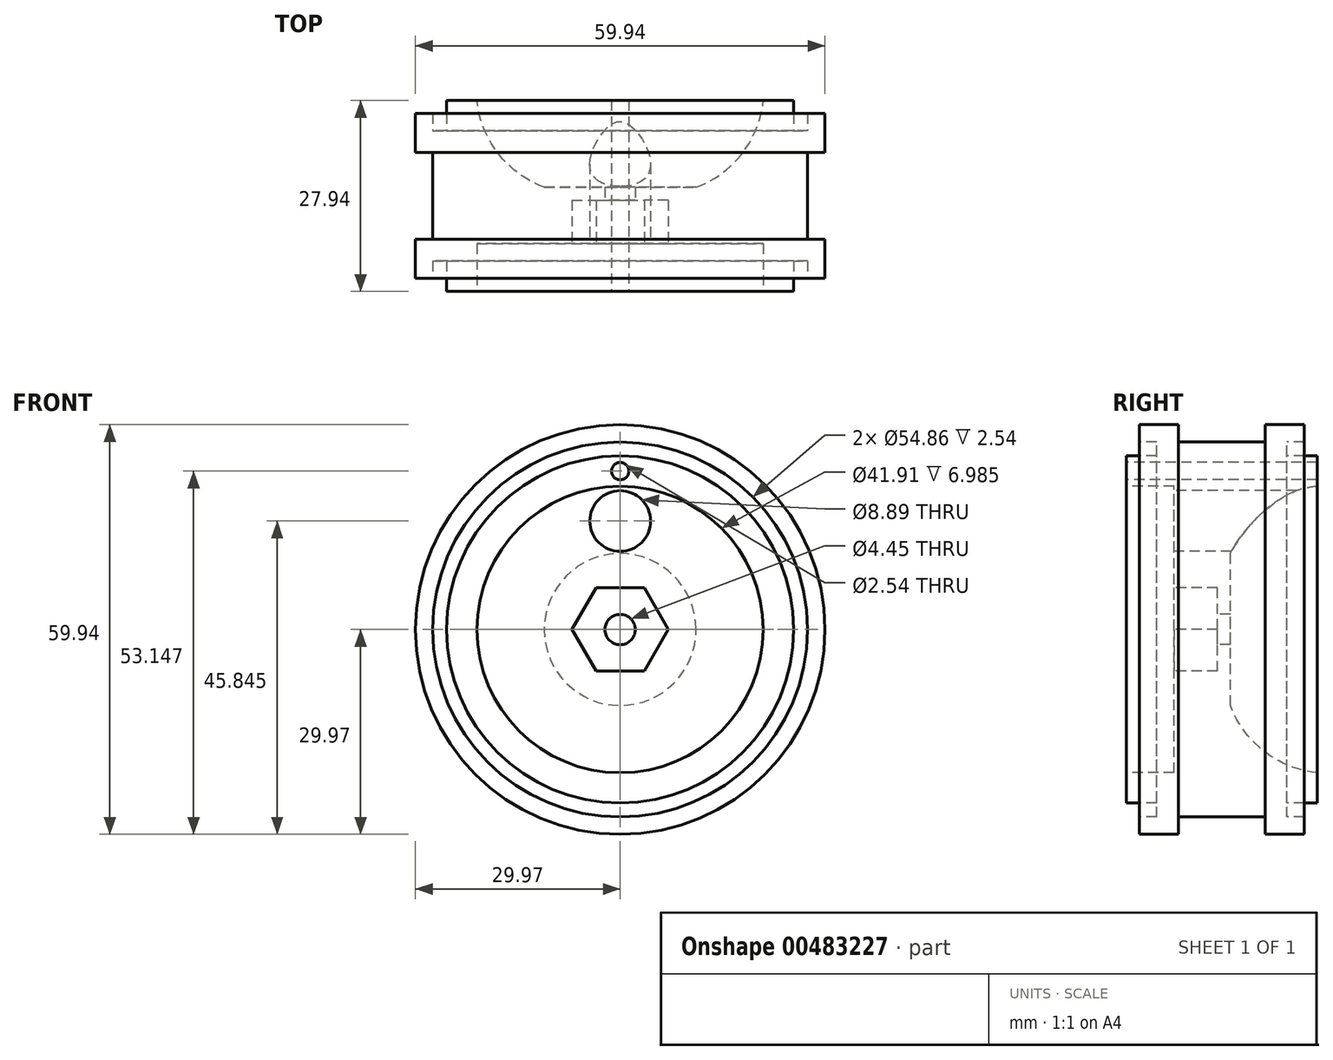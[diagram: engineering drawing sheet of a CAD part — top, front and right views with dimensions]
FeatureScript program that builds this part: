
annotation { "Feature Type Name" : "Feature", "Feature Type Description" : "" }
export const myFeature = defineFeature(function(context is Context, id is Id, definition is map)
    precondition{}
    {
        {
            var Q0;
            Q0=qCreatedBy(makeId("Front.planeOp"),FACE);
            var sketch = newSketch(context, id + "F0", { "sketchPlane" : qUnion([Q0])});
            skCircle(sketch, "E0", {"center": v(0, 0) * mm, "radius": 11.11 * mm});
            skSolve(sketch);
        }
        {
            var Q0;
            Q0=makeQuery(id+"F0.imprint","IMPRINT",FACE,{"disambiguationData":[TD([[makeQuery(id+"F0.imprint","IMPRINT",EDGE,{"derivedFrom":sQuery(id+"F0.wireOp",EDGE,"E0")}),1.0]])]});
            extrude(context, id + "F1", {"entities" : qUnion([Q0]), "depth" : 8.25 * mm});
        }
        {
            var Q0;
            Q0=qCreatedBy(makeId("Right.planeOp"),FACE);
            var sketch = newSketch(context, id + "F2", { "sketchPlane" : qUnion([Q0])});
            skLineSegment(sketch, "E1", {"start": v(0, 0) * mm, "end": v(0, 51.8) * mm, "construction": true});
            skLineSegment(sketch, "E2", {"start": v(-21, 0) * mm, "end": v(29.29, 0) * mm, "construction": true});
            skLineSegment(sketch, "E3", {"start": v(-1.27, 0) * mm, "end": v(-1.27, 37.34) * mm, "construction": true});
            skLineSegment(sketch, "E4", {"start": v(-10.8, 25.4) * mm, "end": v(-15.24, 25.4) * mm});
            skLineSegment(sketch, "E5", {"start": v(-10.8, 25.4) * mm, "end": v(-10.8, 27.43) * mm});
            skLineSegment(sketch, "E6", {"start": v(-10.8, 27.43) * mm, "end": v(-13.34, 27.43) * mm});
            skLineSegment(sketch, "E7", {"start": v(-13.34, 27.43) * mm, "end": v(-13.34, 29.97) * mm});
            skLineSegment(sketch, "E8", {"start": v(-13.34, 29.97) * mm, "end": v(-7.62, 29.97) * mm});
            skLineSegment(sketch, "E9", {"start": v(-7.62, 29.97) * mm, "end": v(-7.62, 27.43) * mm});
            skLineSegment(sketch, "E10", {"start": v(-7.62, 27.43) * mm, "end": v(-1.27, 27.43) * mm});
            skLineSegment(sketch, "E11", {"start": v(-15.24, 25.4) * mm, "end": v(-15.24, 20.96) * mm});
            skLineSegment(sketch, "E12.MirrorCS", {"start": v(12.7, 25.4) * mm, "end": v(12.7, 20.96) * mm});
            skLineSegment(sketch, "E13.MirrorCS", {"start": v(8.26, 25.4) * mm, "end": v(12.7, 25.4) * mm});
            skLineSegment(sketch, "E14.MirrorCS", {"start": v(8.26, 25.4) * mm, "end": v(8.26, 27.43) * mm});
            skLineSegment(sketch, "E15.MirrorCS", {"start": v(8.26, 27.43) * mm, "end": v(10.8, 27.43) * mm});
            skLineSegment(sketch, "E16.MirrorCS", {"start": v(10.8, 27.43) * mm, "end": v(10.8, 29.97) * mm});
            skLineSegment(sketch, "E17.MirrorCS", {"start": v(10.8, 29.97) * mm, "end": v(5.08, 29.97) * mm});
            skLineSegment(sketch, "E18.MirrorCS", {"start": v(5.08, 27.43) * mm, "end": v(-1.27, 27.43) * mm});
            skLineSegment(sketch, "E19.MirrorCS", {"start": v(5.08, 29.97) * mm, "end": v(5.08, 27.43) * mm});
            skArc(sketch, "E20", {"start": v(12.7, 20.96) * mm, "mid": v(4.95, 17.84) * mm, "end": v(0, 11.11) * mm});
            skLineSegment(sketch, "E21", {"start": v(-8.26, 11.11) * mm, "end": v(0, 11.11) * mm});
            skLineSegment(sketch, "E22", {"start": v(-8.26, 11.11) * mm, "end": v(-8.26, 20.96) * mm});
            skLineSegment(sketch, "E23", {"start": v(-15.24, 20.96) * mm, "end": v(-8.26, 20.96) * mm});
            skSolve(sketch);
        }
        {
            var Q0;
            Q0 = qSketchRegion(id + "F2", true);
            var Q1;
            Q1=sQuery(id+"F2.wireOp",EDGE,"E2");
            revolve(context, id + "F3", {"operationType" : NewBodyOperationType.ADD, "entities" : qUnion([Q0]), "axis" : qUnion([Q1]), "revolveType" : RevolveType.FULL});
        }
        {
            var Q0;
            Q0=qCreatedBy(makeId("Right.planeOp"),FACE);
            var sketch = newSketch(context, id + "F4", { "sketchPlane" : qUnion([Q0])});
            skLineSegment(sketch, "E24", {"start": v(-28.78, 0) * mm, "end": v(25.16, 0) * mm, "construction": true});
            skSolve(sketch);
        }
        {
            var Q0;
            Q0=qCreatedBy(makeId("Front.planeOp"),FACE);
            var sketch = newSketch(context, id + "F5", { "sketchPlane" : qUnion([Q0])});
            skCircle(sketch, "E25", {"center": v(0, 15.88) * mm, "radius": 4.45 * mm});
            skCircle(sketch, "E26.0", {"center": v(0, 0) * mm, "radius": 20.96 * mm, "construction": true});
            skSolve(sketch);
        }
        {
            var Q0;
            Q0 = qSketchRegion(id + "F5", true);
            extrude(context, id + "F6", {"entities" : qUnion([Q0]), "operationType" : NewBodyOperationType.REMOVE, "endBound" : BoundingType.THROUGH_ALL, "oppositeDirection" : true, "depth" : 25.4 * mm, "hasSecondDirection" : true, "secondDirectionBound" : SecondDirectionBoundingType.THROUGH_ALL, "secondDirectionOppositeDirection" : false, "secondDirectionDepth" : 25.4 * mm});
        }
        {
            var Q0;
            Q0=makeQuery(id+"F1.opExtrude","CAP_FACE",FACE,{"disambiguationData":[OSD([sQuery(id+"F0.wireOp",EDGE,"E0")])],"isStart":false});
            var sketch = newSketch(context, id + "F7", { "sketchPlane" : qUnion([Q0])});
            skCircle(sketch, "E27.cCircle", {"center": v(0, 0) * mm, "radius": 6.1 * mm, "construction": true});
            skLineSegment(sketch, "E27.0", {"start": v(-3.52, 6.1) * mm, "end": v(3.52, 6.1) * mm});
            skLineSegment(sketch, "E27.1", {"start": v(3.52, 6.1) * mm, "end": v(7.04, 0) * mm});
            skLineSegment(sketch, "E27.2", {"start": v(7.04, 0) * mm, "end": v(3.52, -6.1) * mm});
            skLineSegment(sketch, "E27.3", {"start": v(3.52, -6.1) * mm, "end": v(-3.52, -6.1) * mm});
            skLineSegment(sketch, "E27.4", {"start": v(-3.52, -6.1) * mm, "end": v(-7.04, 0) * mm});
            skLineSegment(sketch, "E27.5", {"start": v(-7.04, 0) * mm, "end": v(-3.52, 6.1) * mm});
            skPoint(sketch, "E27.0.midPoint", {"position": v(0, 6.1) * mm});
            skSolve(sketch);
        }
        {
            var Q0;
            Q0 = qSketchRegion(id + "F7", true);
            extrude(context, id + "F8", {"entities" : qUnion([Q0]), "operationType" : NewBodyOperationType.REMOVE, "oppositeDirection" : true, "depth" : 6.35 * mm});
        }
        {
            var Q0;
            Q0=makeQuery(id+"F1.opExtrude","CAP_FACE",FACE,{"disambiguationData":[OSD([sQuery(id+"F0.wireOp",EDGE,"E0")])],"isStart":true});
            var sketch = newSketch(context, id + "F9", { "sketchPlane" : qUnion([Q0])});
            skCircle(sketch, "E28", {"center": v(0, 0) * mm, "radius": 2.22 * mm});
            skSolve(sketch);
        }
        {
            var Q0;
            Q0 = qSketchRegion(id + "F9", true);
            extrude(context, id + "F10", {"entities" : qUnion([Q0]), "operationType" : NewBodyOperationType.REMOVE, "endBound" : BoundingType.THROUGH_ALL, "depth" : 25.4 * mm, "hasSecondDirection" : true, "secondDirectionBound" : SecondDirectionBoundingType.THROUGH_ALL, "secondDirectionOppositeDirection" : true, "secondDirectionDepth" : 25.4 * mm});
        }
        {
            var Q0;
            Q0=makeQuery(id+"F3.opRevolve","SWEPT_FACE",FACE,{"disambiguationData":[OSD([sQuery(id+"F2.wireOp",EDGE,"E11")])]});
            var sketch = newSketch(context, id + "F11", { "sketchPlane" : qUnion([Q0])});
            skCircle(sketch, "E29", {"center": v(0, 0) * mm, "radius": 23.18 * mm, "construction": true});
            skCircle(sketch, "E30", {"center": v(0, 23.18) * mm, "radius": 1.27 * mm});
            skCircle(sketch, "E31.0", {"center": v(0, 0) * mm, "radius": 25.4 * mm, "construction": true});
            skCircle(sketch, "E32.0", {"center": v(0, 0) * mm, "radius": 20.96 * mm, "construction": true});
            skSolve(sketch);
        }
        {
            var Q0;
            Q0 = qSketchRegion(id + "F11", true);
            extrude(context, id + "F12", {"entities" : qUnion([Q0]), "operationType" : NewBodyOperationType.REMOVE, "endBound" : BoundingType.THROUGH_ALL, "oppositeDirection" : true, "depth" : 25.4 * mm, "hasSecondDirection" : true, "secondDirectionBound" : SecondDirectionBoundingType.THROUGH_ALL, "secondDirectionOppositeDirection" : false, "secondDirectionDepth" : 25.4 * mm});
        }
    });
